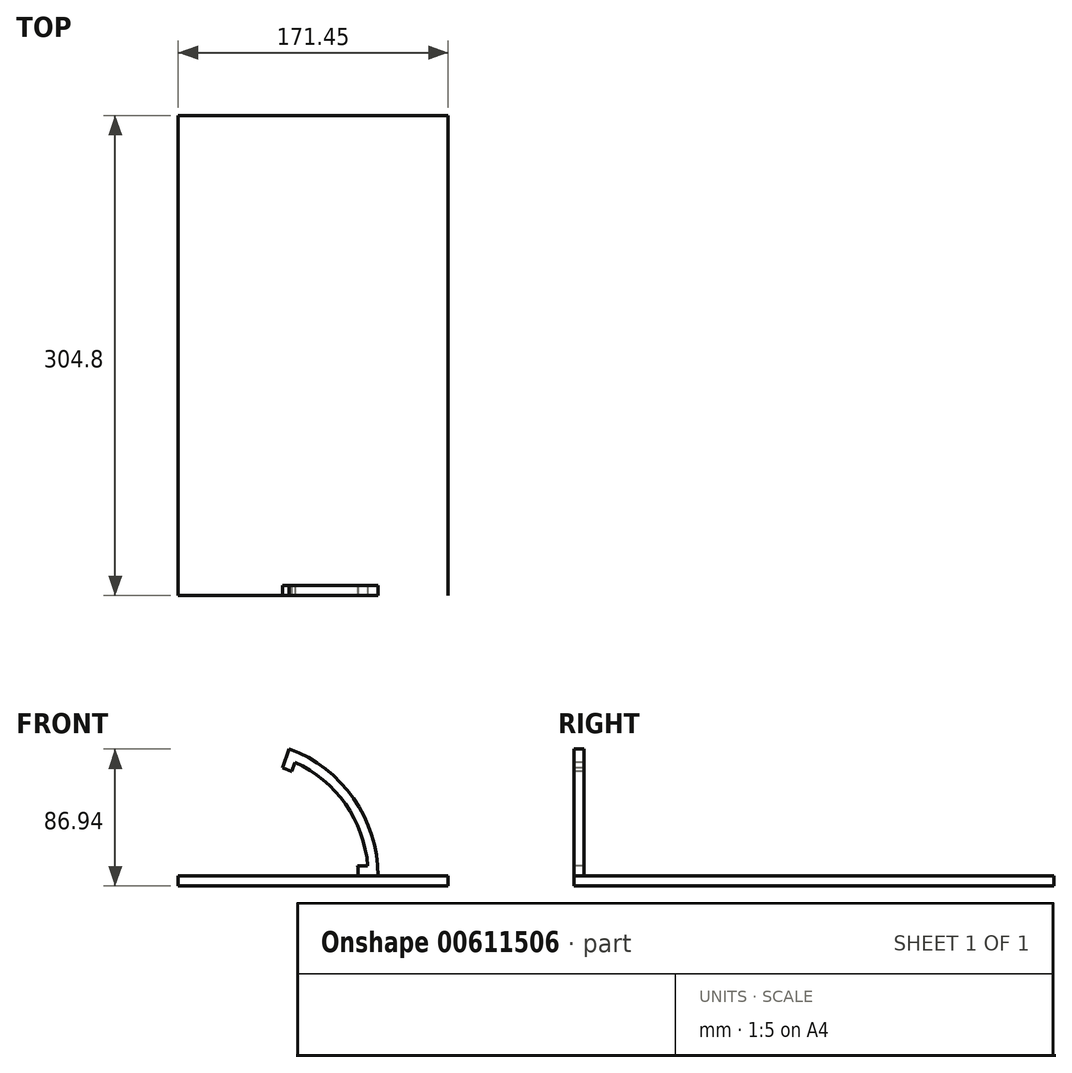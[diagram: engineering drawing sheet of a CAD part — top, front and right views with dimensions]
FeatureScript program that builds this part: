
annotation { "Feature Type Name" : "Feature", "Feature Type Description" : "" }
export const myFeature = defineFeature(function(context is Context, id is Id, definition is map)
    precondition{}
    {
        {
            var Q0;
            Q0=qCreatedBy(makeId("Front.planeOp"),FACE);
            var sketch = newSketch(context, id + "F0", { "sketchPlane" : qUnion([Q0])});
            skLineSegment(sketch, "E0.bottom", {"start": v(-81.5, -29.13) * mm, "end": v(89.95, -29.13) * mm});
            skLineSegment(sketch, "E0.top", {"start": v(-81.5, -22.78) * mm, "end": v(32.8, -22.78) * mm});
            skLineSegment(sketch, "E0.left", {"start": v(-81.5, -29.13) * mm, "end": v(-81.5, -22.78) * mm});
            skLineSegment(sketch, "E0.right", {"start": v(89.95, -29.13) * mm, "end": v(89.95, -22.78) * mm});
            skPoint(sketch, "E1", {"position": v(-40.23, -22.78) * mm});
            skPoint(sketch, "E2", {"position": v(-11.65, -22.78) * mm});
            skPoint(sketch, "E3", {"position": v(-11.01, 57.81) * mm});
            skPoint(sketch, "E4", {"position": v(45.5, -22.78) * mm});
            skLineSegment(sketch, "E5", {"start": v(-11.01, 57.81) * mm, "end": v(-40.23, -22.78) * mm});
            skArc(sketch, "E6", {"start": v(45.5, -22.78) * mm, "mid": v(29.96, 26.43) * mm, "end": v(-11.01, 57.81) * mm});
            skLineSegment(sketch, "E7", {"start": v(-40.23, -22.78) * mm, "end": v(-11.65, -22.78) * mm});
            skLineSegment(sketch, "E8", {"start": v(-11.65, -22.78) * mm, "end": v(45.5, -22.78) * mm});
            skArc(sketch, "E9", {"start": v(39.15, -22.78) * mm, "mid": v(26.53, 20.15) * mm, "end": v(-7.3, 49.44) * mm});
            skArc(sketch, "E10", {"start": v(32.8, -22.78) * mm, "mid": v(19.56, 19.14) * mm, "end": v(-15.34, 45.87) * mm});
            skPoint(sketch, "E11", {"position": v(38.9, -16.43) * mm});
            skPoint(sketch, "E12", {"position": v(-9.48, 43.42) * mm});
            skPoint(sketch, "E13", {"position": v(-7.3, 49.44) * mm});
            skLineSegment(sketch, "E14", {"start": v(-7.3, 49.44) * mm, "end": v(-9.47, 43.45) * mm});
            skArc(sketch, "E15", {"start": v(-7.3, 49.44) * mm, "mid": v(-10.21, 50.7) * mm, "end": v(-13.18, 51.84) * mm});
            skLineSegment(sketch, "E16", {"start": v(-9.47, 43.45) * mm, "end": v(-9.47, 43.44) * mm});
            skLineSegment(sketch, "E17", {"start": v(-15.34, 45.87) * mm, "end": v(-15.34, 45.87) * mm});
            skLineSegment(sketch, "E18", {"start": v(-9.48, 43.44) * mm, "end": v(-9.48, 43.43) * mm});
            skLineSegment(sketch, "E19", {"start": v(-9.47, 43.44) * mm, "end": v(-9.48, 43.44) * mm});
            skLineSegment(sketch, "E20", {"start": v(-9.47, 43.45) * mm, "end": v(-9.48, 43.43) * mm});
            skLineSegment(sketch, "E21", {"start": v(-9.47, 43.45) * mm, "end": v(-9.48, 43.42) * mm});
            skPoint(sketch, "E22", {"position": v(32.52, -16.43) * mm});
            skLineSegment(sketch, "E23", {"start": v(38.9, -16.43) * mm, "end": v(35.7, -16.43) * mm});
            skLineSegment(sketch, "E24", {"start": v(19.07, 29.99) * mm, "end": v(19.07, 29.99) * mm});
            skPoint(sketch, "E25", {"position": v(35.97, -22.78) * mm});
            skPoint(sketch, "E26", {"position": v(35.7, -16.43) * mm});
            skPoint(sketch, "E26.positionSnap0", {"position": v(35.7, -16.43) * mm});
            skLineSegment(sketch, "E27", {"start": v(35.7, -16.43) * mm, "end": v(32.52, -16.43) * mm});
            skArc(sketch, "E28", {"start": v(35.7, -16.43) * mm, "mid": v(22.16, 20.97) * mm, "end": v(-8.39, 46.45) * mm});
            skLineSegment(sketch, "E29.trimOffspring", {"start": v(35.97, -22.78) * mm, "end": v(89.95, -22.78) * mm});
            skSolve(sketch);
        }
        {
            var Q0;
            Q0=qCreatedBy(makeId("Front.planeOp"),FACE);
            var sketch = newSketch(context, id + "F1", { "sketchPlane" : qUnion([Q0])});
            skLineSegment(sketch, "E30", {"start": v(0, 0) * mm, "end": v(57.15, 0) * mm});
            skPoint(sketch, "E31", {"position": v(28.58, 0) * mm});
            skLineSegment(sketch, "E32", {"start": v(28.58, 0) * mm, "end": v(28.58, 25.4) * mm});
            skLineSegment(sketch, "E33", {"start": v(28.58, 25.4) * mm, "end": v(28.58, 15.88) * mm});
            skCircle(sketch, "E34", {"center": v(28.58, 15.88) * mm, "radius": 3.18 * mm});
            skLineSegment(sketch, "E35", {"start": v(57.15, 0) * mm, "end": v(57.15, 6.35) * mm});
            skLineSegment(sketch, "E36", {"start": v(57.15, 6.35) * mm, "end": v(0, 6.35) * mm, "construction": true});
            skLineSegment(sketch, "E37", {"start": v(0, 6.35) * mm, "end": v(0, 0) * mm});
            skLineSegment(sketch, "E38", {"start": v(28.58, 25.4) * mm, "end": v(57.15, 6.35) * mm});
            skLineSegment(sketch, "E39", {"start": v(28.58, 25.4) * mm, "end": v(0, 6.35) * mm});
            skSolve(sketch);
        }
        {
            var Q0;
            {var subQ1=sQuery(id+"F0.wireOp",EDGE,"E6");Q0=makeQuery(id+"F0.imprint","IMPRINT",FACE,{"disambiguationData":[TD([[makeQuery(id+"F0.imprint","IMPRINT",EDGE,{"derivedFrom":subQ1}),1.0]])]});}
            var Q1;
            {var subQ4=sQuery(id+"F0.wireOp",EDGE,"E14");Q1=makeQuery(id+"F0.imprint","IMPRINT",FACE,{"disambiguationData":[TD([[makeQuery(id+"F0.imprint","IMPRINT",EDGE,{"derivedFrom":subQ4}),-1.0]])]});}
            var Q2;
            {var subQ4=sQuery(id+"F0.wireOp",EDGE,"E7");Q2=makeQuery(id+"F0.imprint","IMPRINT",FACE,{"disambiguationData":[TD([[makeQuery(id+"F0.imprint","IMPRINT",EDGE,{"derivedFrom":subQ4}),1.0]])]});}
            var Q3;
            {var subQ5=sQuery(id+"F0.wireOp",EDGE,"E23");Q3=makeQuery(id+"F0.imprint","IMPRINT",FACE,{"disambiguationData":[TD([[makeQuery(id+"F0.imprint","IMPRINT",EDGE,{"derivedFrom":subQ5}),1.0]])]});}
            extrude(context, id + "F2", {"entities" : qUnion([Q0, Q1, Q2, Q3]), "oppositeDirection" : true, "depth" : 6.35 * mm, "offsetDistance" : 25.4 * mm});
        }
        {
            var Q0;
            Q0=makeQuery(id+"F0.imprint","IMPRINT",FACE,{"disambiguationData":[TD([[makeQuery(id+"F0.imprint","IMPRINT",EDGE,{"derivedFrom":sQuery(id+"F0.wireOp",EDGE,"E0.bottom")}),1.0]])]});
            var Q1;
            Q1 = qSketchRegion(id + "F4", true);
            extrude(context, id + "F3", {"entities" : qUnion([Q0, Q1]), "oppositeDirection" : true, "depth" : 304.8 * mm, "offsetDistance" : 25.4 * mm, "hasDraft" : true, "draftAngle" : 0 * degree});
        }
        {
            var Q0;
            Q0 = qSketchRegion(id + "F0", true);
            var sketch = newSketch(context, id + "F4", { "sketchPlane" : qUnion([Q0])});
            skSolve(sketch);
        }
        {
            var Q0;
            Q0 = qSketchRegion(id + "F0", true);
            var sketch = newSketch(context, id + "F5", { "sketchPlane" : qUnion([Q0])});
            skPoint(sketch, "E40", {"position": v(24.1, -43.77) * mm});
            skSolve(sketch);
        }
    });
